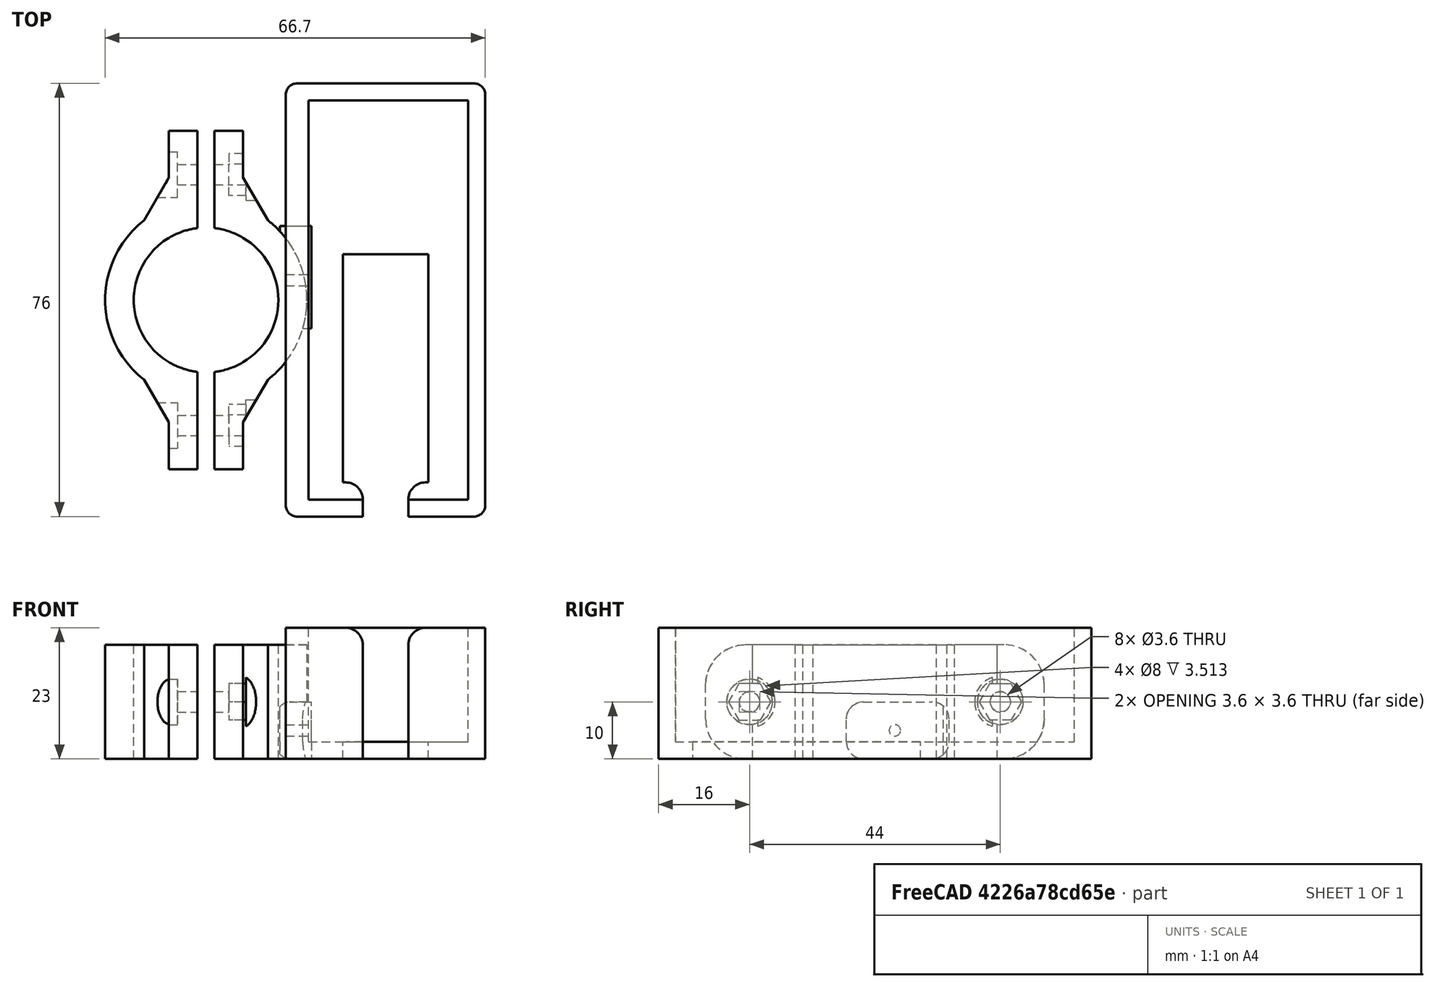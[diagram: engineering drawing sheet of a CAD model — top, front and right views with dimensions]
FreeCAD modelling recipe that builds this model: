
FCSTD DOCUMENT  (FreeCAD 0.18.4R)
Label: power_sock_holder
License: All rights reserved
LicenseURL: http://en.wikipedia.org/wiki/All_rights_reserved
objects: Part::Box×5, Part::Fillet×3, Part::MultiFuse×3, PartDesign::FeatureBase×2, PartDesign::Body×2, Part::Cut×2, Part::Feature×1, Spreadsheet::Sheet×1, Part::Cylinder×1
note: 19 computed .brp shape members not serialized (recipe doc carries the construction recipe); baked Part::Feature solids carry a one-line shape summary decoded from their .brp

FEATURE [Part::Feature] Cut023015001  label="tube block"
  Placement = pos=(-14,38,0) rot=(0,0,-1;1.5708rad)
  shape: bbox 35.4 x 59.4 x 20 mm, 58 faces, 2 solids (baked)
FEATURE [Spreadsheet::Sheet] Spreadsheet  label="p"
  cells = A1=internal_width; B1(internal_width)=70; A2=internal_depth; B2(internal_depth)=28; A3=bottom_hole_depth; B3(bottom_hole_depth)=15; A4=bottom_internal_height; B4(bottom_internal_height)=20; A5=wall; B5(wall)=3; A6=back_wall; B6(back_wall)=4; A7=bottom_hole_width; B7(bottom_hole_width)=40; A8=bottom_hole_width_off; B8(bottom_hole_width_off)=3; A9=bottom_hole_back_off; B9(bottom_hole_back_off)=6; A10=hole_to_side_off; B10(hole_to_side_off)==(33.6 - 26.6) / 2; A11=wire_size; B11(wire_size)=8
FEATURE [Part::Box] Box  label="outer cube"
  AttacherType = Attacher::AttachEngine3D
  Height = 23
  Length = 35
  Width = 76
  expr: Height = p.bottom_internal_height + p.wall
  expr: Width = p.internal_width + 2 * p.wall
  expr: Length = p.internal_depth + p.back_wall + p.wall
FEATURE [Part::Box] Box001  label="inner cube"
  AttacherType = Attacher::AttachEngine3D
  Height = 120
  Length = 28
  Placement = pos=(4,3,3) rot=(0,0,1;0rad)
  Width = 70
  expr: Placement.Base.y = p.wall
  expr: Placement.Base.x = p.back_wall
  expr: Placement.Base.z = p.wall
  expr: Height = p.bottom_internal_height + 100
  expr: Width = p.internal_width
  expr: Length = p.internal_depth
FEATURE [Part::Fillet] Fillet  label="outer fillet"
  Base = -> Box
  Edges = 4 edges r=2: [Edge1,Edge3,Edge5,Edge7]
FEATURE [Part::Box] Box002  label="bottom_hole_cube"
  AttacherType = Attacher::AttachEngine3D
  Height = 10
  Length = 15
  Placement = pos=(10,6,0) rot=(0,0,1;0rad)
  Width = 40
  expr: Placement.Base.x = p.bottom_hole_back_off + p.back_wall
  expr: Placement.Base.y = p.bottom_hole_width_off + p.wall
  expr: Length = p.bottom_hole_depth
  expr: Width = p.bottom_hole_width
FEATURE [PartDesign::FeatureBase] Clone
  BaseFeature = -> Cut023015001
  Placement = pos=(-14,38,0) rot=(0,0,-1;1.5708rad)
FEATURE [PartDesign::Body] Body  label="tube block clone"
  BaseFeature = -> Cut023015001
  Group = -> [Clone]
  Origin = -> Origin
  Tip = -> Clone
FEATURE [PartDesign::FeatureBase] Clone001
  BaseFeature = -> Cut023015001
  Placement = pos=(-14,38,0) rot=(0,0,-1;1.5708rad)
FEATURE [PartDesign::Body] Body001  label="tube block clone001"
  BaseFeature = -> Cut023015001
  Group = -> [Clone001]
  Origin = -> Origin001
  Tip = -> Clone001
FEATURE [Part::Box] Box003  label="Cube"
  AttacherType = Attacher::AttachEngine3D
  Height = 10
  Length = 5.5
  Width = 18
FEATURE [Part::Fillet] Fillet001
  Base = -> Box003
  Edges = 4 edges r=3: [Edge9,Edge10,Edge11,Edge12]
  Placement = pos=(-1,33,0) rot=(0,0,1;0rad)
FEATURE [Part::Cylinder] Cylinder  label="screw hole"
  Angle = 360
  AttacherType = Attacher::AttachEngine3D
  Height = 10
  Placement = pos=(0,41.5,5) rot=(0,1,0;1.5708rad)
  Radius = 1
  expr: Placement.Base.y = 38 + p.hole_to_side_off
FEATURE [Part::MultiFuse] Fusion001  label="top fusion"
  Shapes = -> [Body001,Fillet001]
FEATURE [Part::Cut] Cut023015002  label="top cut"
  Base = -> Fusion001
  Tool = -> Cylinder
FEATURE [Part::Box] Box004  label="wire extraction cube"
  AttacherType = Attacher::AttachEngine3D
  Height = 23
  Length = 8
  Placement = pos=(13.5,0,0) rot=(0,0,1;0rad)
  Width = 40
  expr: Height = p.bottom_internal_height + p.wall
  expr: Placement.Base.x = p.bottom_hole_back_off + p.back_wall + (p.bottom_hole_depth - p.wire_size) / 2
  expr: Length = p.wire_size
  expr: Width = p.bottom_hole_width
FEATURE [Part::MultiFuse] Fusion  label="extraction fusion"
  Shapes = -> [Box002,Box001,Box004]
FEATURE [Part::Cut] Cut  label="bottom cut"
  Base = -> Fillet
  Tool = -> Fusion
FEATURE [Part::Fillet] Fillet002  label="bottom cut fillet"
  Base = -> Cut
  Edges = 4 edges r=3: [Edge11,Edge17,Edge44,Edge56]
FEATURE [Part::MultiFuse] Fusion002  label="bottom fusion"
  Shapes = -> [Fillet002,Body]
